# Revit family: Sanitary_Toilet-Seats_Sanindusa_Urby-60-F-D-Close-Coupled-Toilet
name_source: partatom
category: Plumbing Fixtures
revit_build: Autodesk Revit 2018 (Build: 20170223_1515(x64)
units: mm (PartAtom-declared; Revit-internal decimal feet)

## family parameters
Always vertical = Yes
Cut with Voids When Loaded = No
Host = Wall
OmniClass Number = 23.45.00.00
OmniClass Title = Sanitary, Laundry, and Cleaning Equipment
Part Type = Normal
Room Calculation Point = No
Round Connector Dimension = Use Diameter
Shared = No

## types (1)
- Sanindusa
    AssetType = Fixed
    CodePerformance = EN 997:2012 CL 1 - 6 A
    Color = White
    Constituents = Compatible toilet seats (not included): 2403100-Toilet seat urb.y clipoff with slow close system; 2401100-Toilet seat urb.y clipoff. Compatible cisterns (not included): 140171004LM - Urb.y 60 bottom water supply connection cistern with dual flush mechanism; 140173004LM - Urb.y 60 side water supply connection cistern with dual flush mechanism. 24-fixing kit (included)
    Cost = 0 $
    Description = Soil appliance for the disposal of excrement.
    DrainSize = 90 mm  [stored 0.295276 ft]
    Edition number = 1
    Features = Domestic and commercial use. Versatile timeless design. Seats with clipoff system easy to clean and slow close option. Back to wall WC.
    Finish = gloss
    InletDiameter = 50 mm  [stored 0.164042 ft]
    Installation Instructions = https://www.tec.sanindusa.pt
    InstallationDate = 1900-12-31T23:59:59
    ManufacturerName = Sanindusa
    ManufacturerURL = www.tec.sanindusa.pt
    Material = Vitreous China
    ModelNumber = 140023004
    ModelReference = Urb.y
    Name = Urb.y 60 F|D close coupled toilet
    NominalHeight = 390 mm  [stored 1.27953 ft]
    NominalLength = 356 mm  [stored 1.16798 ft]
    NominalWidth = 605 mm  [stored 1.98491 ft]
    Product Guid = 2d2fc8ea-dd6e-4bb0-b29b-9fff1351743d
    Product data url = https://bimobject.com
    ProductInformation = https://www.tec.sanindusa.pt
    ProductionYear = 2018
    Size = 356x605x390
    SustainabilityPerformance = n/a
n/a
    URL = www.tec.sanindusa.pt
    Uniclass2015Code = Pr_40_20_93_94
    Uniclass2015Title = WC pans
    Uniclass2015Version = Products v1.6
    Version = 1
    WarrantyDescription = https://www.tec.sanindusa.pt
    WarrantyDurationParts = 5
    WarrantyDurationUnit = year
    WarrantyStartDate = 1900-12-31T23:59:59
    Weight = 31.10 kg

note: [stored X ft] marks values corroborated as IEEE doubles in the binary element streams (Revit-internal decimal feet)

## geometry (parser evidence)
native form markers: Sweep x6
no freeform markers — native parametric forms only
